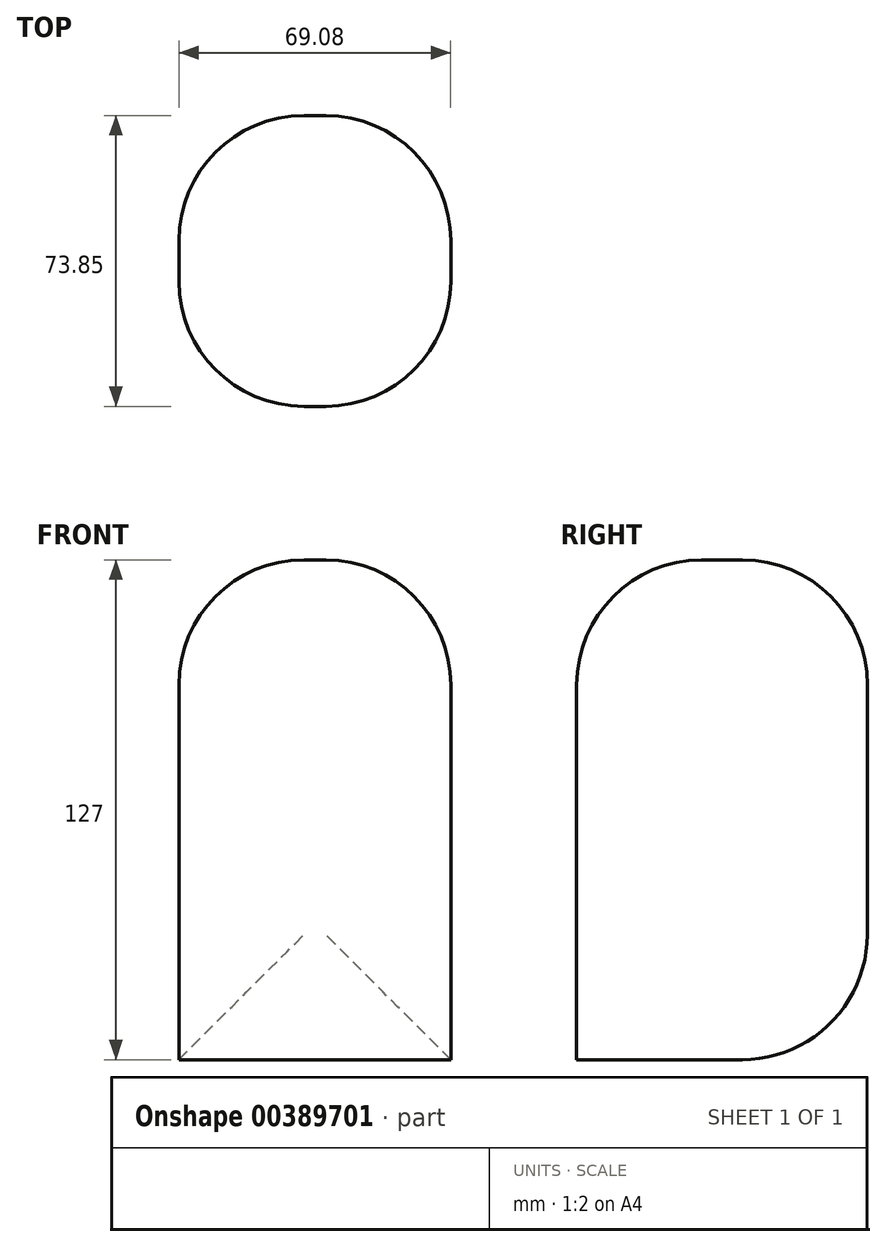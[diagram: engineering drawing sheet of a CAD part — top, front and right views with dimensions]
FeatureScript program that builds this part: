
annotation { "Feature Type Name" : "Feature", "Feature Type Description" : "" }
export const myFeature = defineFeature(function(context is Context, id is Id, definition is map)
    precondition{}
    {
        {
            var Q0;
            Q0=qCreatedBy(makeId("Top.planeOp"),FACE);
            var sketch = newSketch(context, id + "F0", { "sketchPlane" : qUnion([Q0])});
            skLineSegment(sketch, "E0.bottom", {"start": v(-39.2, -31.74) * mm, "end": v(29.87, -31.74) * mm});
            skLineSegment(sketch, "E0.top", {"start": v(-39.2, 42.11) * mm, "end": v(29.87, 42.11) * mm});
            skLineSegment(sketch, "E0.left", {"start": v(-39.2, -31.74) * mm, "end": v(-39.2, 42.11) * mm});
            skLineSegment(sketch, "E0.right", {"start": v(29.87, -31.74) * mm, "end": v(29.87, 42.11) * mm});
            skSolve(sketch);
        }
        {
            var Q0;
            Q0=makeQuery(id+"F0.imprint","IMPRINT",FACE,{"disambiguationData":[TD([[makeQuery(id+"F0.imprint","IMPRINT",EDGE,{"derivedFrom":sQuery(id+"F0.wireOp",EDGE,"E0.bottom")}),1.0]])]});
            extrude(context, id + "F1", {"entities" : qUnion([Q0]), "depth" : 127 * mm});
        }
        {
            var Q0;
            Q0=makeQuery(id+"F1.opExtrude","CAP_EDGE",EDGE,{"disambiguationData":[OSD([sQuery(id+"F0.wireOp",EDGE,"E0.right")])],"isStart":false});
            var Q1;
            Q1=makeQuery(id+"F1.opExtrude","CAP_EDGE",EDGE,{"disambiguationData":[OSD([sQuery(id+"F0.wireOp",EDGE,"E0.bottom")])],"isStart":false});
            var Q2;
            Q2=makeQuery(id+"F1.opExtrude","CAP_EDGE",EDGE,{"disambiguationData":[OSD([sQuery(id+"F0.wireOp",EDGE,"E0.left")])],"isStart":false});
            var Q3;
            Q3=makeQuery(id+"F1.opExtrude","CAP_EDGE",EDGE,{"disambiguationData":[OSD([sQuery(id+"F0.wireOp",EDGE,"E0.top")])],"isStart":false});
            var Q4;
            Q4=makeQuery(id+"F1.opExtrude","SWEPT_EDGE",EDGE,{"disambiguationData":[OSD([sQuery(id+"F0.wireOp",EDGE,"E0.bottom"),sQuery(id+"F0.wireOp",EDGE,"E0.right")])]});
            var Q5;
            Q5=makeQuery(id+"F1.opExtrude","SWEPT_EDGE",EDGE,{"disambiguationData":[OSD([sQuery(id+"F0.wireOp",EDGE,"E0.bottom"),sQuery(id+"F0.wireOp",EDGE,"E0.left")])]});
            var Q6;
            Q6=makeQuery(id+"F1.opExtrude","SWEPT_FACE",FACE,{"disambiguationData":[OSD([sQuery(id+"F0.wireOp",EDGE,"E0.top")])]});
            fillet(context, id + "F2", {"entities" : qUnion([Q0, Q1, Q2, Q3, Q4, Q5, Q6]), "radius" : 31.75 * mm, "tangentPropagation" : true, "allowEdgeOverflow" : false});
        }
    });
